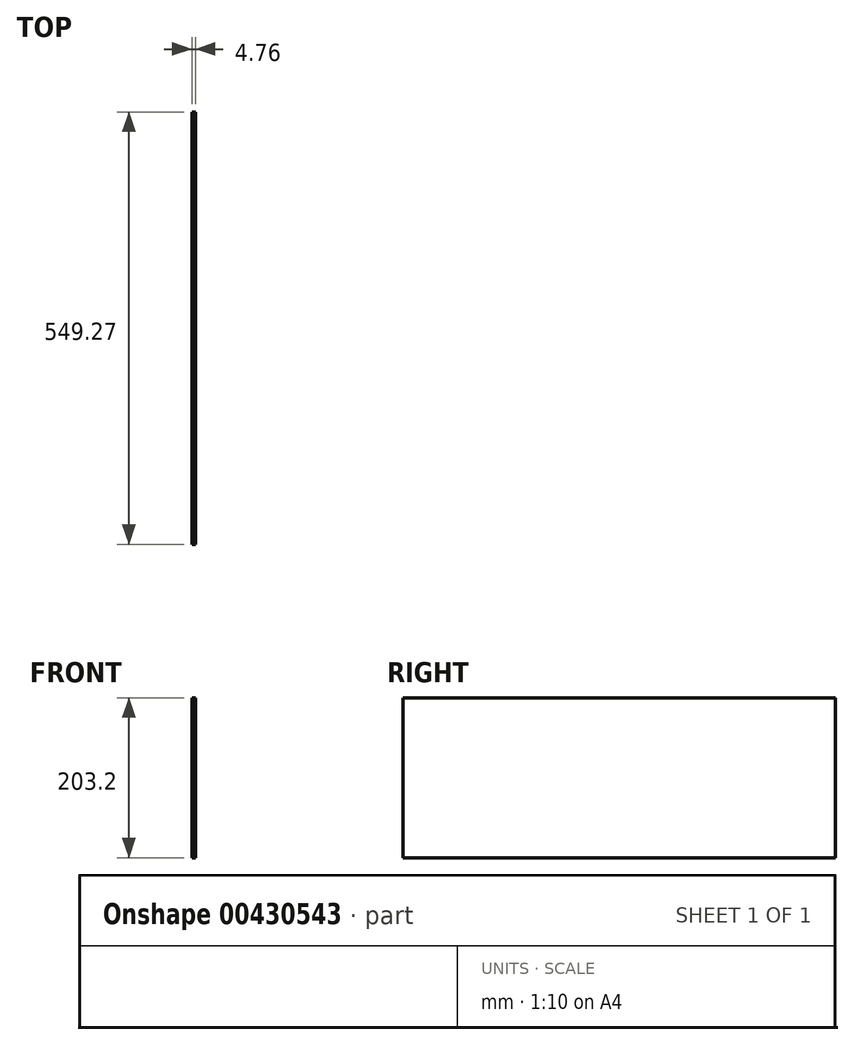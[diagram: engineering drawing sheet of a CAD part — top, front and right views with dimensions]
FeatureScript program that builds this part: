
annotation { "Feature Type Name" : "Feature", "Feature Type Description" : "" }
export const myFeature = defineFeature(function(context is Context, id is Id, definition is map)
    precondition{}
    {
        {
            var Q0;
            Q0=qCreatedBy(makeId("Right.planeOp"),FACE);
            var sketch = newSketch(context, id + "F0", { "sketchPlane" : qUnion([Q0])});
            skLineSegment(sketch, "E0.bottom", {"start": v(-227.5, 65.92) * mm, "end": v(321.77, 65.92) * mm});
            skLineSegment(sketch, "E0.top", {"start": v(-227.5, -137.28) * mm, "end": v(321.77, -137.28) * mm});
            skLineSegment(sketch, "E0.left", {"start": v(-227.5, 65.92) * mm, "end": v(-227.5, -137.28) * mm});
            skLineSegment(sketch, "E0.right", {"start": v(321.77, 65.92) * mm, "end": v(321.77, -137.28) * mm});
            skSolve(sketch);
        }
        {
            var Q0;
            Q0=makeQuery(id+"F0.imprint","IMPRINT",FACE,{"disambiguationData":[TD([[makeQuery(id+"F0.imprint","IMPRINT",EDGE,{"derivedFrom":sQuery(id+"F0.wireOp",EDGE,"E0.bottom")}),-1.0]])]});
            extrude(context, id + "F1", {"entities" : qUnion([Q0]), "depth" : 4.76 * mm});
        }
    });
